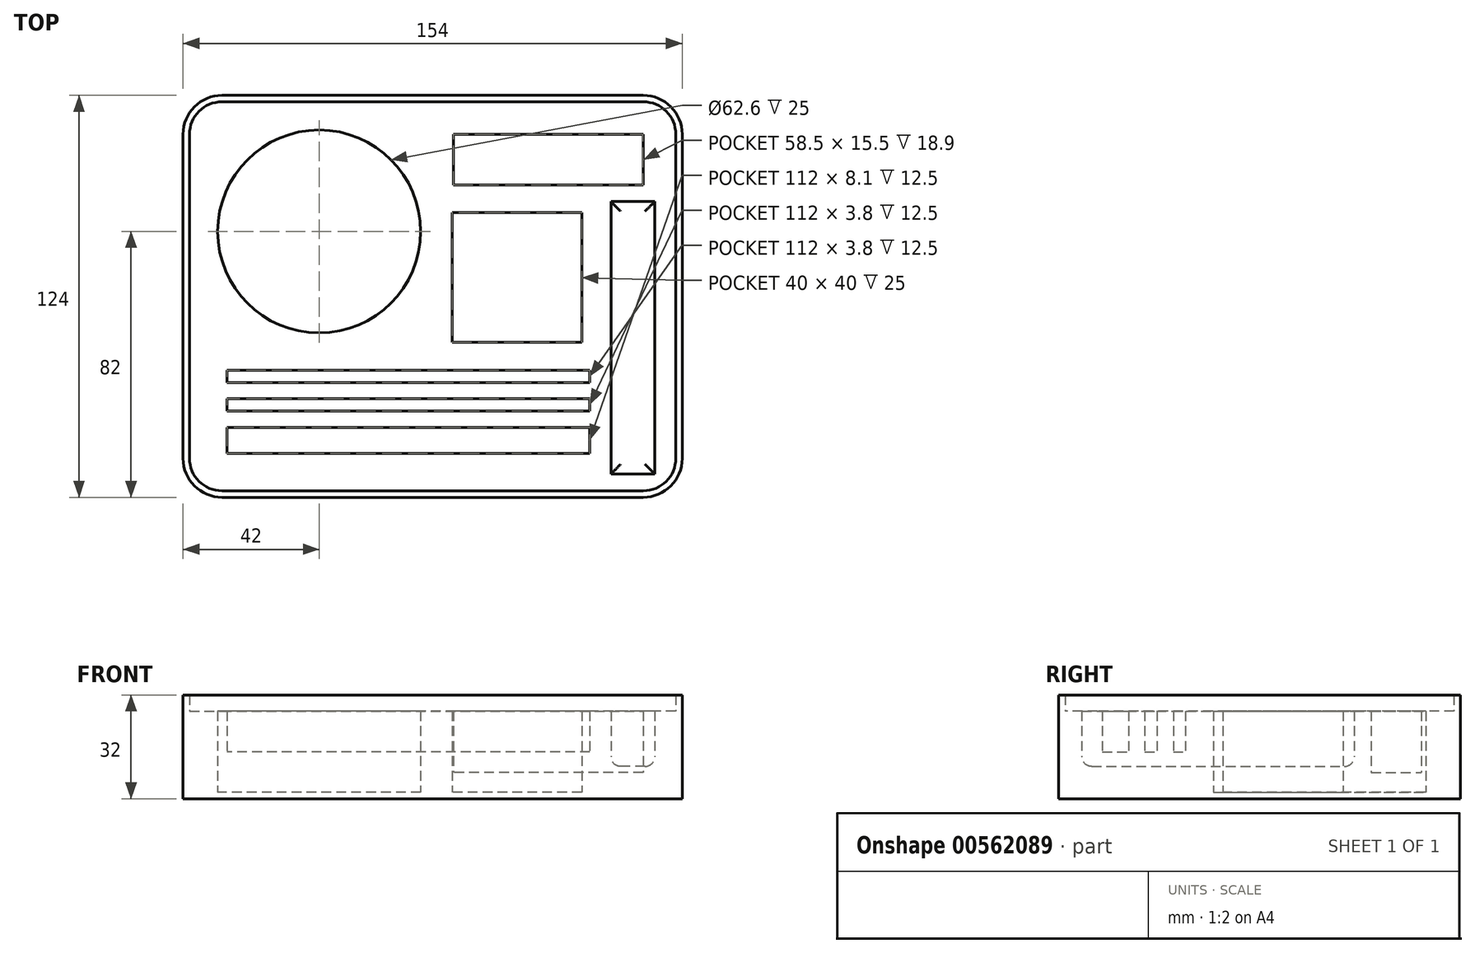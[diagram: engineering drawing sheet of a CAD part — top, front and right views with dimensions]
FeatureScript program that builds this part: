
annotation { "Feature Type Name" : "Feature", "Feature Type Description" : "" }
export const myFeature = defineFeature(function(context is Context, id is Id, definition is map)
    precondition{}
    {
        {
            var Q0;
            Q0=qCreatedBy(makeId("Top.planeOp"),FACE);
            var sketch = newSketch(context, id + "F0", { "sketchPlane" : qUnion([Q0])});
            skLineSegment(sketch, "E0.bottom", {"start": v(-65, 60) * mm, "end": v(65, 60) * mm});
            skLineSegment(sketch, "E0.top", {"start": v(-65, -60) * mm, "end": v(65, -60) * mm});
            skLineSegment(sketch, "E0.left", {"start": v(-75, 50) * mm, "end": v(-75, -50) * mm});
            skLineSegment(sketch, "E0.right", {"start": v(75, 50) * mm, "end": v(75, -50) * mm});
            skPoint(sketch, "E0.middle", {"position": v(0, 0) * mm});
            skLineSegment(sketch, "E1.bottom", {"start": v(48.5, -48.5) * mm, "end": v(-63.5, -48.5) * mm});
            skLineSegment(sketch, "E1.top", {"start": v(48.5, -40.4) * mm, "end": v(-63.5, -40.4) * mm});
            skLineSegment(sketch, "E1.left", {"start": v(48.5, -48.5) * mm, "end": v(48.5, -40.4) * mm});
            skLineSegment(sketch, "E1.right", {"start": v(-63.5, -48.5) * mm, "end": v(-63.5, -40.4) * mm});
            skCircle(sketch, "E2", {"center": v(-35, 20) * mm, "radius": 31.3 * mm});
            skLineSegment(sketch, "E3.bottom", {"start": v(48.5, -35.4) * mm, "end": v(-63.5, -35.4) * mm});
            skLineSegment(sketch, "E3.top", {"start": v(48.5, -31.6) * mm, "end": v(-63.5, -31.6) * mm});
            skLineSegment(sketch, "E3.left", {"start": v(48.5, -35.4) * mm, "end": v(48.5, -31.6) * mm});
            skLineSegment(sketch, "E3.right", {"start": v(-63.5, -35.4) * mm, "end": v(-63.5, -31.6) * mm});
            skLineSegment(sketch, "E4.bottom", {"start": v(48.5, -26.6) * mm, "end": v(-63.5, -26.6) * mm});
            skLineSegment(sketch, "E4.top", {"start": v(48.5, -22.8) * mm, "end": v(-63.5, -22.8) * mm});
            skLineSegment(sketch, "E4.left", {"start": v(48.5, -26.6) * mm, "end": v(48.5, -22.8) * mm});
            skLineSegment(sketch, "E4.right", {"start": v(-63.5, -26.6) * mm, "end": v(-63.5, -22.8) * mm});
            skLineSegment(sketch, "E5.bottom", {"start": v(64.9, 34.4) * mm, "end": v(6.4, 34.4) * mm});
            skLineSegment(sketch, "E5.top", {"start": v(64.9, 49.9) * mm, "end": v(6.4, 49.9) * mm});
            skLineSegment(sketch, "E5.left", {"start": v(64.9, 34.4) * mm, "end": v(64.9, 49.9) * mm});
            skLineSegment(sketch, "E5.right", {"start": v(6.4, 34.4) * mm, "end": v(6.4, 49.9) * mm});
            skPoint(sketch, "E5.middle", {"position": v(35.65, 42.15) * mm});
            skLineSegment(sketch, "E6.bottom", {"start": v(68.5, -54.8) * mm, "end": v(55, -54.8) * mm});
            skLineSegment(sketch, "E6.top", {"start": v(68.5, 29.2) * mm, "end": v(55, 29.2) * mm});
            skLineSegment(sketch, "E6.left", {"start": v(68.5, -54.8) * mm, "end": v(68.5, 29.2) * mm});
            skLineSegment(sketch, "E6.right", {"start": v(55, -54.8) * mm, "end": v(55, 29.2) * mm});
            skPoint(sketch, "E6.middle", {"position": v(61.75, -12.8) * mm});
            skPoint(sketch, "E7.visualSharp", {"position": v(-75, 60) * mm});
            skArc(sketch, "E7.filletArc", {"start": v(-65, 60) * mm, "mid": v(-72.07, 57.07) * mm, "end": v(-75, 50) * mm});
            skPoint(sketch, "E8.visualSharp", {"position": v(-75, -60) * mm});
            skArc(sketch, "E8.filletArc", {"start": v(-75, -50) * mm, "mid": v(-72.07, -57.07) * mm, "end": v(-65, -60) * mm});
            skPoint(sketch, "E9.visualSharp", {"position": v(75, -60) * mm});
            skArc(sketch, "E9.filletArc", {"start": v(65, -60) * mm, "mid": v(72.07, -57.07) * mm, "end": v(75, -50) * mm});
            skPoint(sketch, "E10.visualSharp", {"position": v(75, 60) * mm});
            skArc(sketch, "E10.filletArc", {"start": v(75, 50) * mm, "mid": v(72.07, 57.07) * mm, "end": v(65, 60) * mm});
            skArc(sketch, "E11.0", {"start": v(-65, 62) * mm, "mid": v(-73.49, 58.49) * mm, "end": v(-77, 50) * mm});
            skLineSegment(sketch, "E11.1", {"start": v(-77, 50) * mm, "end": v(-77, -50) * mm});
            skLineSegment(sketch, "E11.2", {"start": v(-65, 62) * mm, "end": v(65, 62) * mm});
            skArc(sketch, "E11.3", {"start": v(-77, -50) * mm, "mid": v(-73.49, -58.49) * mm, "end": v(-65, -62) * mm});
            skArc(sketch, "E11.4", {"start": v(77, 50) * mm, "mid": v(73.49, 58.49) * mm, "end": v(65, 62) * mm});
            skLineSegment(sketch, "E11.5", {"start": v(77, 50) * mm, "end": v(77, -50) * mm});
            skArc(sketch, "E11.6", {"start": v(65, -62) * mm, "mid": v(73.49, -58.49) * mm, "end": v(77, -50) * mm});
            skLineSegment(sketch, "E11.7", {"start": v(-65, -62) * mm, "end": v(65, -62) * mm});
            skLineSegment(sketch, "E12.bottom", {"start": v(46.03, -14.2) * mm, "end": v(6.03, -14.2) * mm});
            skLineSegment(sketch, "E12.top", {"start": v(46.03, 25.8) * mm, "end": v(6.03, 25.8) * mm});
            skLineSegment(sketch, "E12.left", {"start": v(46.03, -14.2) * mm, "end": v(46.03, 25.8) * mm});
            skLineSegment(sketch, "E12.right", {"start": v(6.03, -14.2) * mm, "end": v(6.03, 25.8) * mm});
            skSolve(sketch);
        }
        {
            var Q0;
            Q0=makeQuery(id+"F0.imprint","IMPRINT",FACE,{"disambiguationData":[TD([[makeQuery(id+"F0.imprint","IMPRINT",EDGE,{"derivedFrom":sQuery(id+"F0.wireOp",EDGE,"E0.bottom")}),1.0]])]});
            extrude(context, id + "F1", {"entities" : qUnion([Q0]), "depth" : 32 * mm, "offsetDistance" : 25 * mm});
        }
        {
            var Q0;
            Q0=makeQuery(id+"F0.imprint","IMPRINT",FACE,{"disambiguationData":[TD([[makeQuery(id+"F0.imprint","IMPRINT",EDGE,{"derivedFrom":sQuery(id+"F0.wireOp",EDGE,"E0.bottom")}),-1.0]])]});
            extrude(context, id + "F2", {"entities" : qUnion([Q0]), "operationType" : NewBodyOperationType.ADD, "depth" : 27 * mm, "offsetDistance" : 25 * mm});
        }
        {
            var Q0;
            Q0=makeQuery(id+"F0.imprint","IMPRINT",FACE,{"disambiguationData":[TD([[makeQuery(id+"F0.imprint","IMPRINT",EDGE,{"derivedFrom":sQuery(id+"F0.wireOp",EDGE,"E2")}),1.0]])]});
            extrude(context, id + "F3", {"entities" : qUnion([Q0]), "operationType" : NewBodyOperationType.ADD, "depth" : 2 * mm, "offsetDistance" : 25 * mm});
        }
        {
            var Q0;
            Q0=makeQuery(id+"F0.imprint","IMPRINT",FACE,{"disambiguationData":[TD([[makeQuery(id+"F0.imprint","IMPRINT",EDGE,{"derivedFrom":sQuery(id+"F0.wireOp",EDGE,"E5.bottom")}),-1.0]])]});
            extrude(context, id + "F4", {"entities" : qUnion([Q0]), "operationType" : NewBodyOperationType.ADD, "depth" : 8.1 * mm, "offsetDistance" : 25 * mm});
        }
        {
            var Q0;
            Q0=makeQuery(id+"F0.imprint","IMPRINT",FACE,{"disambiguationData":[TD([[makeQuery(id+"F0.imprint","IMPRINT",EDGE,{"derivedFrom":sQuery(id+"F0.wireOp",EDGE,"E6.bottom")}),-1.0]])]});
            extrude(context, id + "F5", {"entities" : qUnion([Q0]), "operationType" : NewBodyOperationType.ADD, "depth" : 10 * mm, "offsetDistance" : 25 * mm});
        }
        {
            var Q0;
            Q0=makeQuery(id+"F5.opExtrude","CAP_FACE",FACE,{"disambiguationData":[OSD([sQuery(id+"F0.wireOp",EDGE,"E6.bottom"),sQuery(id+"F0.wireOp",EDGE,"E6.top"),sQuery(id+"F0.wireOp",EDGE,"E6.left"),sQuery(id+"F0.wireOp",EDGE,"E6.right")])],"isStart":false});
            fillet(context, id + "F6", {"entities" : qUnion([Q0]), "radius" : 3 * mm, "tangentPropagation" : true, "allowEdgeOverflow" : false});
        }
        {
            var Q0;
            Q0=makeQuery(id+"F0.imprint","IMPRINT",FACE,{"disambiguationData":[TD([[makeQuery(id+"F0.imprint","IMPRINT",EDGE,{"derivedFrom":sQuery(id+"F0.wireOp",EDGE,"E1.bottom")}),-1.0]])]});
            var Q1;
            Q1=makeQuery(id+"F0.imprint","IMPRINT",FACE,{"disambiguationData":[TD([[makeQuery(id+"F0.imprint","IMPRINT",EDGE,{"derivedFrom":sQuery(id+"F0.wireOp",EDGE,"E3.bottom")}),-1.0]])]});
            var Q2;
            Q2=makeQuery(id+"F0.imprint","IMPRINT",FACE,{"disambiguationData":[TD([[makeQuery(id+"F0.imprint","IMPRINT",EDGE,{"derivedFrom":sQuery(id+"F0.wireOp",EDGE,"E4.bottom")}),-1.0]])]});
            extrude(context, id + "F7", {"entities" : qUnion([Q0, Q1, Q2]), "operationType" : NewBodyOperationType.ADD, "depth" : 14.5 * mm, "offsetDistance" : 25 * mm});
        }
        {
            var Q0;
            Q0=makeQuery(id+"F0.imprint","IMPRINT",FACE,{"disambiguationData":[TD([[makeQuery(id+"F0.imprint","IMPRINT",EDGE,{"derivedFrom":sQuery(id+"F0.wireOp",EDGE,"E12.bottom")}),-1.0]])]});
            extrude(context, id + "F8", {"entities" : qUnion([Q0]), "operationType" : NewBodyOperationType.ADD, "depth" : 2 * mm, "offsetDistance" : 25 * mm});
        }
    });
